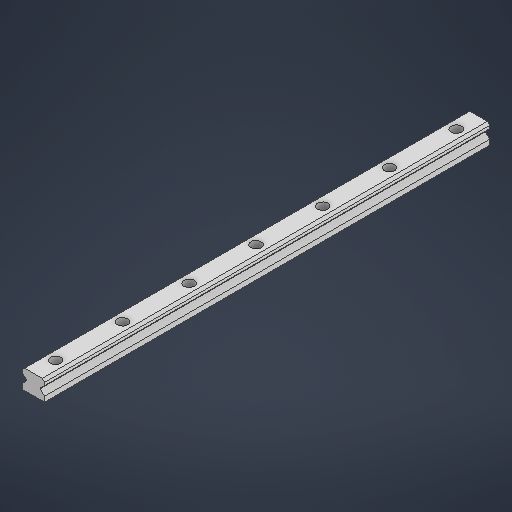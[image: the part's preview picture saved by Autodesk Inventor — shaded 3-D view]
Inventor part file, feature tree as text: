
AUTODESK INVENTOR PART (.ipt)
format: ipt  version: 2025.1 (Build 291241000, 241)  size: 240,128 bytes
history: native  units: mm
features: extrude x3, sketch x2, pattern_linear x1
ambient origin geometry x8: Origin, YZ Plane, XZ Plane, XY Plane, X Axis, Y Axis, Z Axis, Center Point
bodies: Solid1 (feature_tree)
feature tree (6):
  extrude  "Extrusion1"  Depth=20.0mm
  sketch  "Sketch2"  dims[d2=4.6mm d3=8.5mm d8=135.0deg d9=0.5mm d10=135.0deg d11=2.5mm d12=400.0mm d13=0.0mm d14=20.0mm d15=60.0mm d16=9.5mm d17=6.0mm d18=8.5mm d19=0.0mm d20=8.5mm d21=0.0mm d22=90.0mm d24=60.0mm]
  extrude  "Extrusion2"  Depth=8.5mm
  extrude  "Extrusion3"  TaperAngle=135.0deg  [1 undecoded]
  pattern_linear  "Rectangular Pattern1"  Spacing1=0.5mm  [1 undecoded]
  sketch  "Sketch1"  dims[d0=17.5mm d1=20.0mm]
note: 2 required parameter values undecoded (feature->parameter linkage not recoverable at this tier; creation-order binding heuristic only, values carry confidence <= 0.55)
